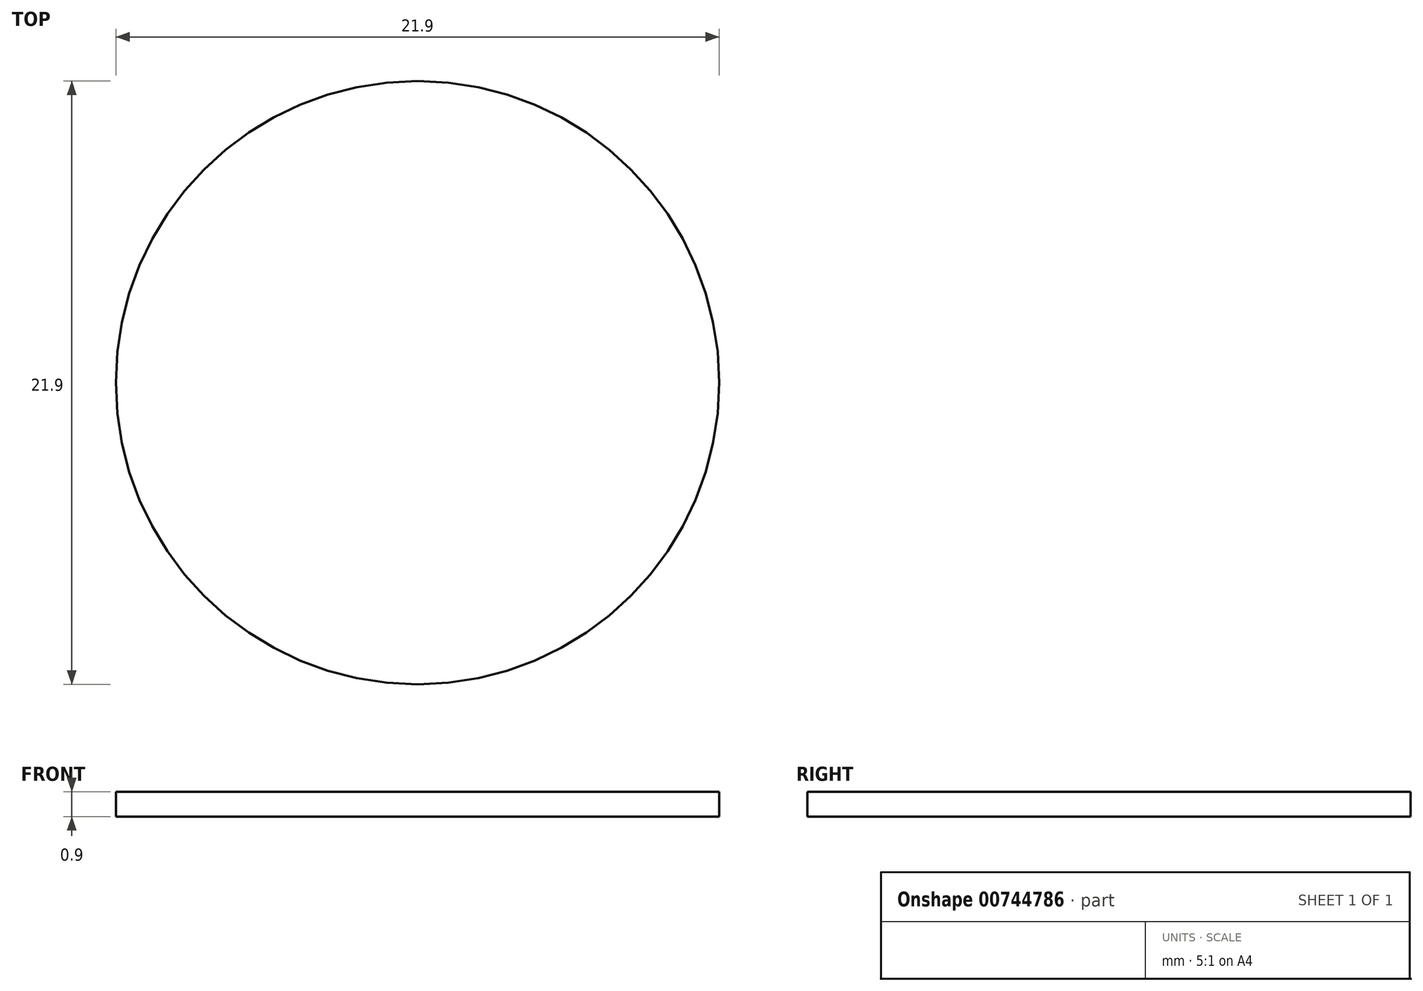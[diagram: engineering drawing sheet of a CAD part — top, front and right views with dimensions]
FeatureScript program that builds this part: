
annotation { "Feature Type Name" : "Feature", "Feature Type Description" : "" }
export const myFeature = defineFeature(function(context is Context, id is Id, definition is map)
    precondition{}
    {
        {
            var Q0;
            Q0=qCreatedBy(makeId("Top.planeOp"),FACE);
            var sketch = newSketch(context, id + "F0", { "sketchPlane" : qUnion([Q0])});
            skCircle(sketch, "E0", {"center": v(0, 0) * mm, "radius": 10.95 * mm});
            skSolve(sketch);
        }
        {
            var Q0;
            Q0=qSketchRegion(id+"F0",true);
            extrude(context, id + "F1", {"entities" : qUnion([Q0]), "depth" : .9 * mm, "offsetDistance" : 25 * mm});
        }
    });
